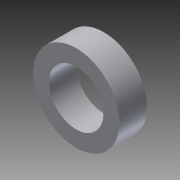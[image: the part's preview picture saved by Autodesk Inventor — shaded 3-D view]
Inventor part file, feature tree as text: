
AUTODESK INVENTOR PART (.ipt)
format: ipt  version: 2014 (Build 180170000, 170)  size: 86,016 bytes
history: native  units: in
note: dims shown in document units (in); Inventor stores cm internally (conversion verified against a paired STEP export)
features: extrude x1
ambient origin geometry x8: Origin, YZ Plane, XZ Plane, XY Plane, X Axis, Y Axis, Z Axis, Center Point
bodies: Solid1 (feature_tree)
feature tree (1):
  extrude  "Extrusion1"  Depth=0.63in
